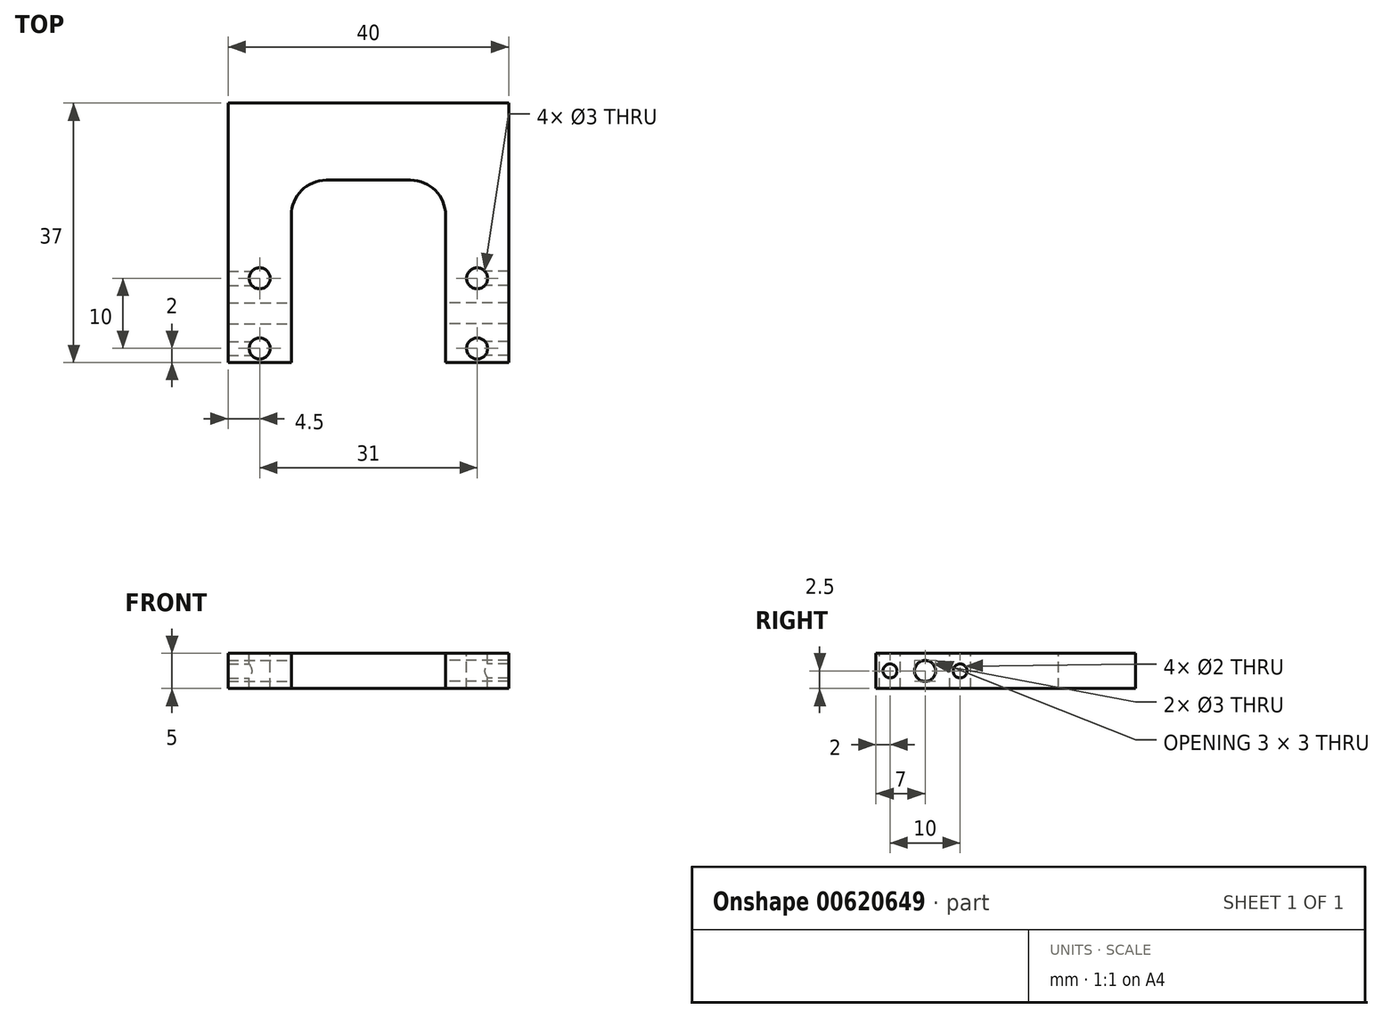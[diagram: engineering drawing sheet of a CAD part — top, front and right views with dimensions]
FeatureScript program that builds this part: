
annotation { "Feature Type Name" : "Feature", "Feature Type Description" : "" }
export const myFeature = defineFeature(function(context is Context, id is Id, definition is map)
    precondition{}
    {
        {
            var Q0;
            Q0=qCreatedBy(makeId("Top.planeOp"),FACE);
            var sketch = newSketch(context, id + "F0", { "sketchPlane" : qUnion([Q0])});
            skLineSegment(sketch, "E0.bottom", {"start": v(0, 7) * mm, "end": v(20, 7) * mm});
            skLineSegment(sketch, "E0.top", {"start": v(0, 44) * mm, "end": v(20, 44) * mm});
            skLineSegment(sketch, "E0.right", {"start": v(20, 7) * mm, "end": v(20, 44) * mm});
            skPoint(sketch, "E1", {"position": v(0, 7) * mm});
            skCircle(sketch, "E2", {"center": v(15.5, 9) * mm, "radius": 1.5 * mm});
            skCircle(sketch, "E3", {"center": v(15.5, 19) * mm, "radius": 1.5 * mm});
            skLineSegment(sketch, "E4", {"start": v(0, 7) * mm, "end": v(0, 44) * mm});
            skLineSegment(sketch, "E5", {"start": v(11, 7) * mm, "end": v(11, 33) * mm});
            skLineSegment(sketch, "E6", {"start": v(11, 33) * mm, "end": v(0, 33) * mm});
            skSolve(sketch);
        }
        {
            var Q0;
            {var subQ1=sQuery(id+"F0.wireOp",EDGE,"E0.top");Q0=makeQuery(id+"F0.imprint","IMPRINT",FACE,{"disambiguationData":[TD([[makeQuery(id+"F0.imprint","IMPRINT",EDGE,{"derivedFrom":subQ1}),-1.0]])]});}
            var Q1;
            Q1=makeQuery(id+"F0.imprint","IMPRINT",FACE,{"disambiguationData":[TD([[makeQuery(id+"F0.imprint","IMPRINT",EDGE,{"derivedFrom":sQuery(id+"F0.wireOp",EDGE,"E2")}),-1.0]])]});
            var Q2;
            {var subQ3=sQuery(id+"F0.wireOp",EDGE,"vhTgpiIu-4f2N-fcw0-Xi6h-DEbZ4F3tPtaA");Q2=makeQuery(id+"F0.imprint","IMPRINT",FACE,{"disambiguationData":[TD([[makeQuery(id+"F0.imprint","IMPRINT",EDGE,{"derivedFrom":subQ3}),1.0]])]});}
            var Q3;
            {var subQ0=sQuery(id+"F0.wireOp",EDGE,"NSDAVhUq-5Hfi-qhf0-B9wr-upKBhRcVgcbo");Q3=makeQuery(id+"F0.imprint","IMPRINT",FACE,{"disambiguationData":[TD([[makeQuery(id+"F0.imprint","IMPRINT",EDGE,{"derivedFrom":subQ0}),1.0]])]});}
            extrude(context, id + "F1", {"entities" : qUnion([Q0, Q1, Q2, Q3]), "oppositeDirection" : true, "depth" : 5 * mm, "offsetDistance" : 25 * mm});
        }
        {
            var Q0;
            Q0=makeQuery(id+"F1.opExtrude","SWEPT_FACE",FACE,{"disambiguationData":[OSD([sQuery(id+"F0.wireOp",EDGE,"E0.right")])]});
            var sketch = newSketch(context, id + "F2", { "sketchPlane" : qUnion([Q0])});
            skPoint(sketch, "E7", {"position": v(9, -2.5) * mm});
            skPoint(sketch, "E8", {"position": v(19, -2.5) * mm});
            skLineSegment(sketch, "E9", {"start": v(9, -2.5) * mm, "end": v(19, -2.5) * mm, "construction": true});
            skPoint(sketch, "E10", {"position": v(14, -2.5) * mm});
            skSolve(sketch);
        }
        {
            var Q0;
            Q0=sQuery(id+"F2.wireOp",VERTEX,"E7");
            var Q1;
            Q1=sQuery(id+"F2.wireOp",VERTEX,"E8");
            var Q2;
            Q2=makeQuery(id+"F1.opExtrude","SWEPT_BODY",BODY,{"disambiguationData":[OSD([sQuery(id+"F0.wireOp",EDGE,"E0.bottom"),sQuery(id+"F0.wireOp",EDGE,"E0.top"),sQuery(id+"F0.wireOp",EDGE,"E0.right"),sQuery(id+"F0.wireOp",EDGE,"E2"),sQuery(id+"F0.wireOp",EDGE,"E3"),sQuery(id+"F0.wireOp",EDGE,"E4")])]});
            hole(context, id + "F3", {"style" : HoleStyle.SIMPLE, "endStyle" : HoleEndStyle.BLIND, "holeDiameter" : 2 * mm, "majorDiameter" : 5 * mm, "holeDepth" : 5 * mm, "isTappedThrough" : true, "tappedDepth" : 12 * mm, "tapClearance" : 3, "locations" : qUnion([Q0, Q1]), "scope" : qUnion([Q2]), "startStyle" : HoleStartStyle.PART});
        }
        {
            var Q0;
            Q0=makeQuery(id+"F1.opExtrude","SWEPT_EDGE",EDGE,{"disambiguationData":[OSD([sQuery(id+"F0.wireOp",EDGE,"E5"),sQuery(id+"F0.wireOp",EDGE,"E6")])]});
            fillet(context, id + "F4", {"entities" : qUnion([Q0]), "radius" : 5 * mm, "tangentPropagation" : true, "allowEdgeOverflow" : false});
        }
        {
            var Q0;
            Q0=sQuery(id+"F2.wireOp",VERTEX,"E10");
            var Q1;
            Q1=makeQuery(id+"F1.opExtrude","SWEPT_BODY",BODY,{"disambiguationData":[OSD([sQuery(id+"F0.wireOp",EDGE,"E0.bottom"),sQuery(id+"F0.wireOp",EDGE,"E0.top"),sQuery(id+"F0.wireOp",EDGE,"E0.right"),sQuery(id+"F0.wireOp",EDGE,"E2"),sQuery(id+"F0.wireOp",EDGE,"E3"),sQuery(id+"F0.wireOp",EDGE,"E4"),sQuery(id+"F0.wireOp",EDGE,"E5"),sQuery(id+"F0.wireOp",EDGE,"E6")])]});
            hole(context, id + "F5", {"style" : HoleStyle.SIMPLE, "endStyle" : HoleEndStyle.THROUGH, "holeDiameter" : 3 * mm, "majorDiameter" : 5 * mm, "isTappedThrough" : true, "tappedDepth" : 12 * mm, "tapClearance" : 3, "locations" : qUnion([Q0]), "scope" : qUnion([Q1]), "startStyle" : HoleStartStyle.PART});
        }
        {
            var Q0;
            Q0=makeQuery(id+"F1.opExtrude","SWEPT_BODY",BODY,{"disambiguationData":[OSD([sQuery(id+"F0.wireOp",EDGE,"E0.bottom"),sQuery(id+"F0.wireOp",EDGE,"E0.top"),sQuery(id+"F0.wireOp",EDGE,"E0.right"),sQuery(id+"F0.wireOp",EDGE,"E2"),sQuery(id+"F0.wireOp",EDGE,"E3"),sQuery(id+"F0.wireOp",EDGE,"E4")])]});
            var Q1;
            Q1=qCreatedBy(makeId("Right.planeOp"),FACE);
            mirror(context, id + "F6", {"operationType" : NewBodyOperationType.ADD, "entities" : qUnion([Q0]), "mirrorPlane" : qUnion([Q1])});
        }
    });
